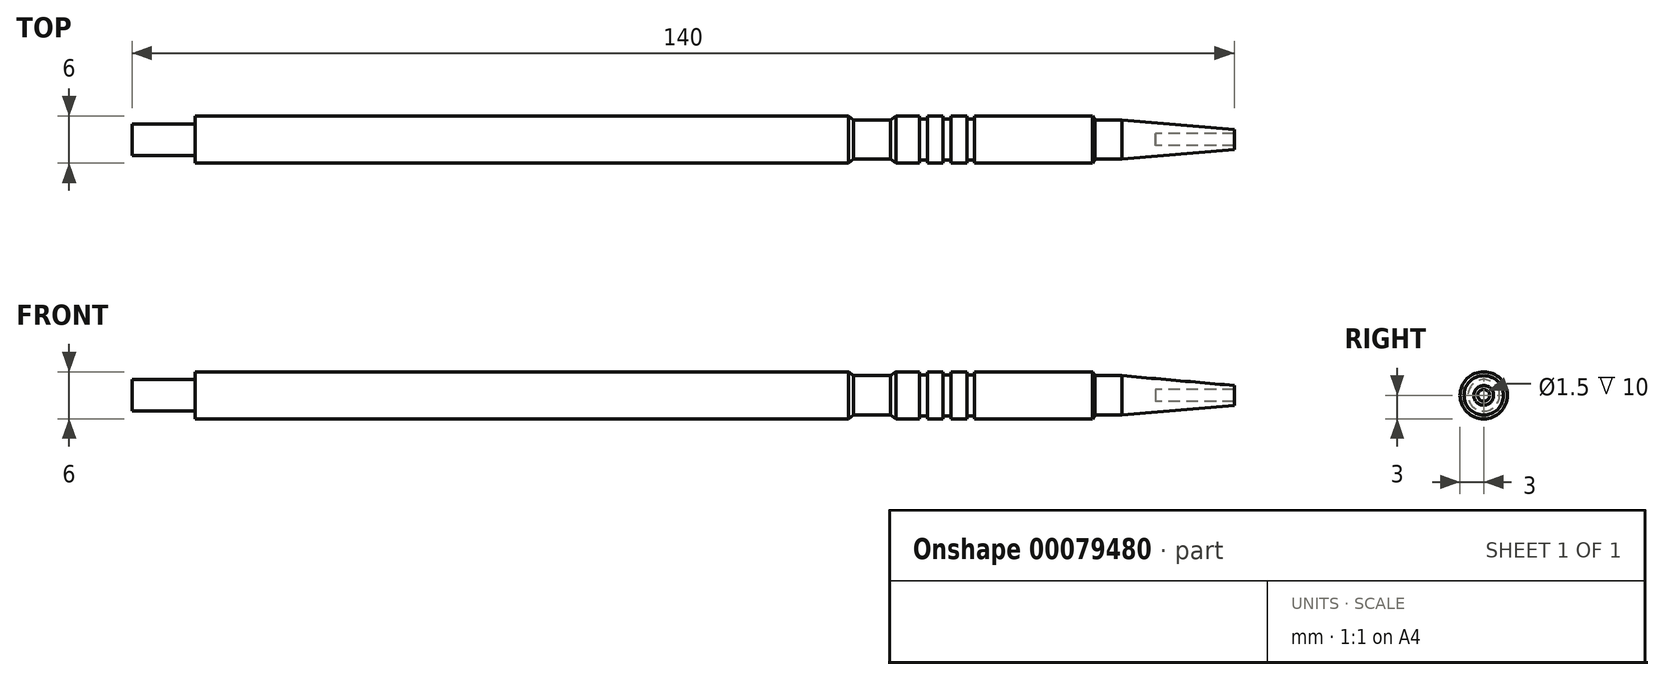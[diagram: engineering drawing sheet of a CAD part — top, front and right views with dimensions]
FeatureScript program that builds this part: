
annotation { "Feature Type Name" : "Feature", "Feature Type Description" : "" }
export const myFeature = defineFeature(function(context is Context, id is Id, definition is map)
    precondition{}
    {
        {
            var Q0;
            Q0=qCreatedBy(makeId("Top.planeOp"),FACE);
            var sketch = newSketch(context, id + "F0", { "sketchPlane" : qUnion([Q0])});
            skLineSegment(sketch, "E0", {"start": v(-85.9, 0) * mm, "end": v(120.31, 0) * mm, "construction": true});
            skLineSegment(sketch, "E1", {"start": v(-89.74, 3) * mm, "end": v(-6.74, 3) * mm});
            skLineSegment(sketch, "E2", {"start": v(24.55, 2.5) * mm, "end": v(27.98, 2.5) * mm});
            skLineSegment(sketch, "E3", {"start": v(27.98, 2.5) * mm, "end": v(42.26, 1.25) * mm});
            skLineSegment(sketch, "E4", {"start": v(42.26, 1.25) * mm, "end": v(42.26, 0.75) * mm});
            skLineSegment(sketch, "E5", {"start": v(42.26, 0.75) * mm, "end": v(32.26, 0.75) * mm});
            skLineSegment(sketch, "E6", {"start": v(32.26, 0.75) * mm, "end": v(32.26, 0) * mm});
            skLineSegment(sketch, "E7", {"start": v(-89.74, 3) * mm, "end": v(-89.74, 2) * mm});
            skLineSegment(sketch, "E8", {"start": v(-89.74, 2) * mm, "end": v(-97.74, 2) * mm});
            skLineSegment(sketch, "E9", {"start": v(-97.74, 2) * mm, "end": v(-97.74, 0) * mm});
            skLineSegment(sketch, "E10", {"start": v(-97.74, 0) * mm, "end": v(32.26, 0) * mm});
            skLineSegment(sketch, "E11", {"start": v(24.55, 2.5) * mm, "end": v(24.26, 3) * mm});
            skLineSegment(sketch, "E12", {"start": v(-6.74, 3) * mm, "end": v(-6.13, 2.5) * mm});
            skLineSegment(sketch, "E13", {"start": v(-6.13, 2.5) * mm, "end": v(-1.43, 2.5) * mm});
            skLineSegment(sketch, "E14", {"start": v(-1.43, 2.5) * mm, "end": v(-0.74, 3) * mm});
            skLineSegment(sketch, "E15", {"start": v(-0.74, 3) * mm, "end": v(24.26, 3) * mm});
            skLineSegment(sketch, "E16", {"start": v(2.26, 3) * mm, "end": v(2.26, 2.6) * mm});
            skLineSegment(sketch, "E17", {"start": v(2.26, 2.6) * mm, "end": v(3.26, 2.6) * mm});
            skLineSegment(sketch, "E18", {"start": v(3.26, 2.6) * mm, "end": v(3.26, 3) * mm});
            skLineSegment(sketch, "E19.0.1.0", {"start": v(5.26, 3) * mm, "end": v(5.26, 2.6) * mm});
            skLineSegment(sketch, "E19.1.1.0", {"start": v(5.26, 2.6) * mm, "end": v(6.26, 2.6) * mm});
            skLineSegment(sketch, "E19.2.1.0", {"start": v(6.26, 2.6) * mm, "end": v(6.26, 3) * mm});
            skLineSegment(sketch, "E19.0.2.0", {"start": v(8.26, 3) * mm, "end": v(8.26, 2.6) * mm});
            skLineSegment(sketch, "E19.1.2.0", {"start": v(8.26, 2.6) * mm, "end": v(9.26, 2.6) * mm});
            skLineSegment(sketch, "E19.2.2.0", {"start": v(9.26, 2.6) * mm, "end": v(9.26, 3) * mm});
            skLineSegment(sketch, "E19.direction1", {"start": v(2.26, 2.6) * mm, "end": v(5.26, 2.6) * mm, "construction": true});
            skSolve(sketch);
        }
        {
            var Q0;
            Q0=makeQuery(id+"F0.imprint","IMPRINT",FACE,{"disambiguationData":[TD([[makeQuery(id+"F0.imprint","IMPRINT",EDGE,{"derivedFrom":sQuery(id+"F0.wireOp",EDGE,"E1")}),-1.0]])]});
            var Q1;
            Q1=sQuery(id+"F0.wireOp",EDGE,"E0");
            revolve(context, id + "F1", {"entities" : qUnion([Q0]), "axis" : qUnion([Q1]), "revolveType" : RevolveType.FULL});
        }
    });
